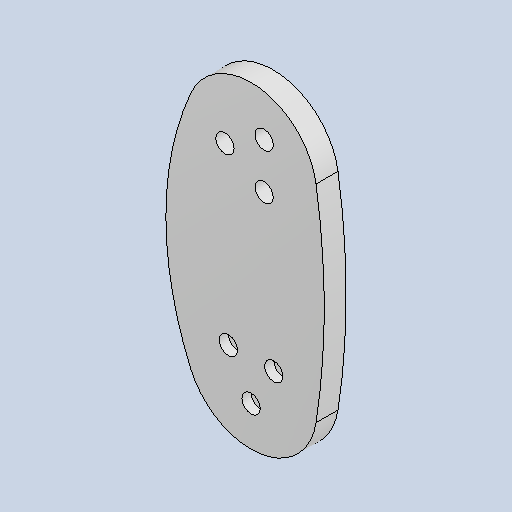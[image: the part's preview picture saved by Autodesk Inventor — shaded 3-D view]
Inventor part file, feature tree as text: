
AUTODESK INVENTOR PART (.ipt)
format: ipt  version: 2023 (Build 270158000, 158)  size: 152,064 bytes
history: native  units: mm
features: other x4, sketch x2
ambient origin geometry x8: Origin, YZ Plane, XZ Plane, XY Plane, X Axis, Y Axis, Z Axis, Center Point
bodies: Solid1 (feature_tree)
feature tree (6):
  other  "クランク_中間.ipt"
  other  "Solid1::クランク_中間.ipt"
  other  "TaggingFeature1"
  sketch  "Sketch2"  dims[d0=10.0mm]
  sketch  "Sketch3"
  other  "sesaku"
